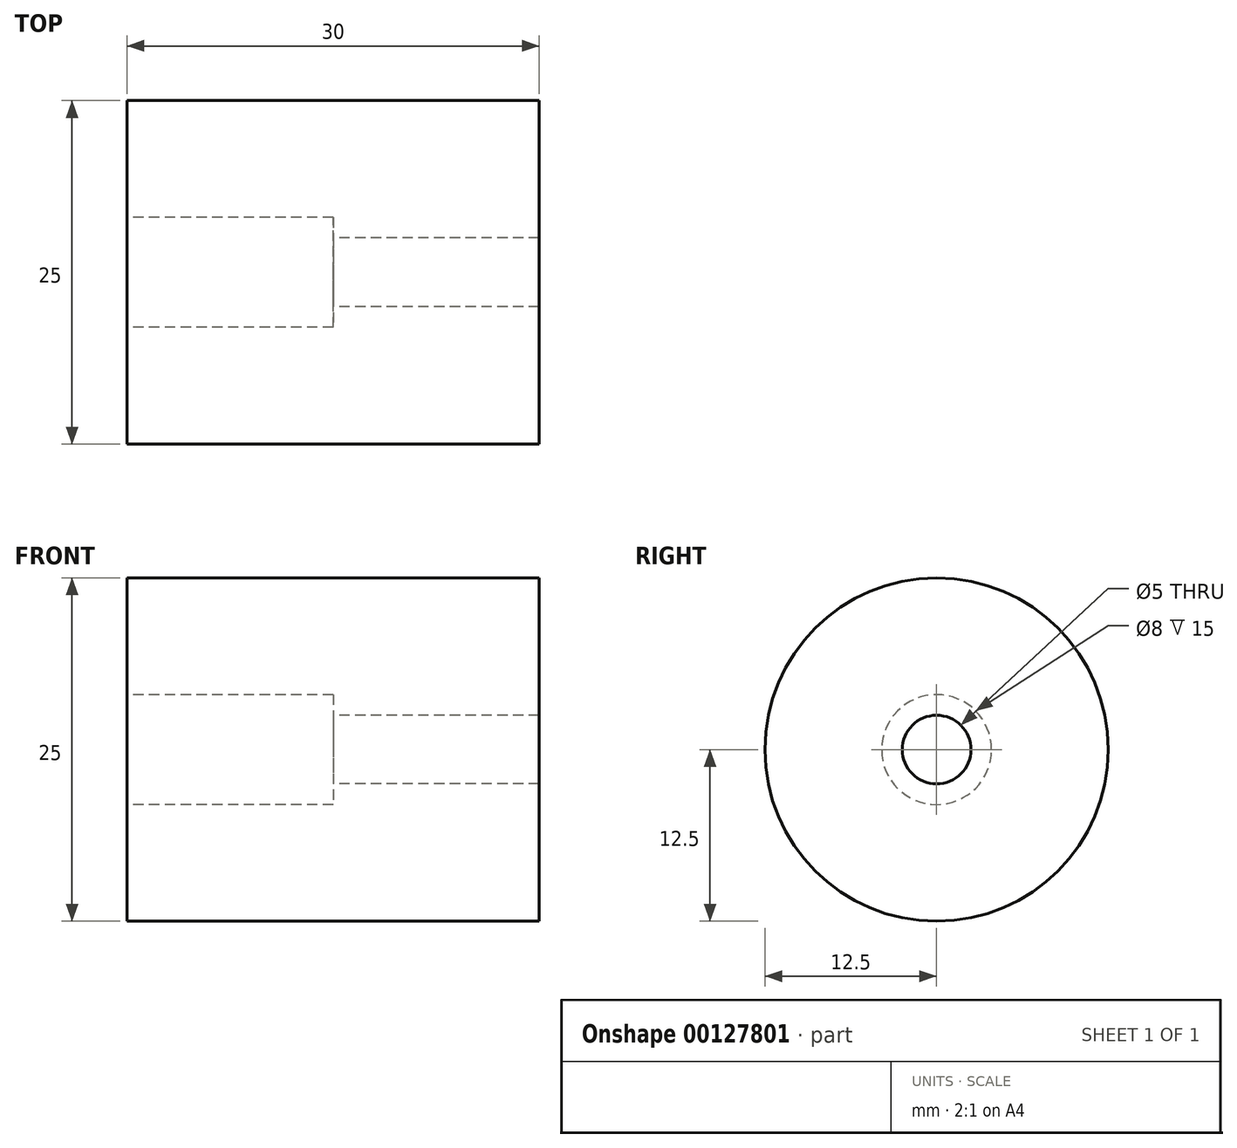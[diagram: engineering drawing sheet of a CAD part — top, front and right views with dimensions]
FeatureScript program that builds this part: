
annotation { "Feature Type Name" : "Feature", "Feature Type Description" : "" }
export const myFeature = defineFeature(function(context is Context, id is Id, definition is map)
    precondition{}
    {
        {
            var Q0;
            Q0=qCreatedBy(makeId("Front.planeOp"),FACE);
            var sketch = newSketch(context, id + "F0", { "sketchPlane" : qUnion([Q0])});
            skLineSegment(sketch, "E0.bottom", {"start": v(-15, 0) * mm, "end": v(15, 0) * mm});
            skLineSegment(sketch, "E0.top", {"start": v(-15, 12.5) * mm, "end": v(15, 12.5) * mm});
            skLineSegment(sketch, "E0.left", {"start": v(-15, 0) * mm, "end": v(-15, 12.5) * mm});
            skLineSegment(sketch, "E0.right", {"start": v(15, 0) * mm, "end": v(15, 12.5) * mm});
            skLineSegment(sketch, "E1", {"start": v(0, 0) * mm, "end": v(-101.73, 0) * mm, "construction": true});
            skSolve(sketch);
        }
        {
            var Q0;
            Q0 = qSketchRegion(id + "F0", true);
            var Q1;
            Q1=sQuery(id+"F0.wireOp",EDGE,"E1");
            revolve(context, id + "F1", {"entities" : qUnion([Q0]), "axis" : qUnion([Q1]), "revolveType" : RevolveType.FULL});
        }
        {
            var Q0;
            Q0=qCreatedBy(makeId("Front.planeOp"),FACE);
            var sketch = newSketch(context, id + "F2", { "sketchPlane" : qUnion([Q0])});
            skLineSegment(sketch, "E2.bottom", {"start": v(0, 0) * mm, "end": v(-15, 0) * mm});
            skLineSegment(sketch, "E2.top", {"start": v(0, 4) * mm, "end": v(-15, 4) * mm});
            skLineSegment(sketch, "E2.right", {"start": v(-15, 0) * mm, "end": v(-15, 4) * mm});
            skLineSegment(sketch, "E3.bottom", {"start": v(0, 0) * mm, "end": v(15, 0) * mm});
            skLineSegment(sketch, "E3.top", {"start": v(0, 2.5) * mm, "end": v(15, 2.5) * mm});
            skLineSegment(sketch, "E3.right", {"start": v(15, 0) * mm, "end": v(15, 2.5) * mm});
            skLineSegment(sketch, "E4", {"start": v(0, 0) * mm, "end": v(-22.87, 0) * mm, "construction": true});
            skLineSegment(sketch, "E5", {"start": v(0, 4) * mm, "end": v(0, 2.5) * mm});
            skSolve(sketch);
        }
        {
            var Q0;
            Q0 = qSketchRegion(id + "F2", true);
            var Q1;
            Q1=sQuery(id+"F2.wireOp",EDGE,"E4");
            revolve(context, id + "F3", {"operationType" : NewBodyOperationType.REMOVE, "entities" : qUnion([Q0]), "axis" : qUnion([Q1]), "revolveType" : RevolveType.FULL, "oppositeDirection" : true});
        }
    });
